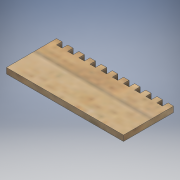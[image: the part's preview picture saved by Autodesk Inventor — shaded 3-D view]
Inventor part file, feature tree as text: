
AUTODESK INVENTOR PART (.ipt)
format: ipt  version: 2017 (Build 210142000, 142)  size: 174,592 bytes
history: native  units: mm
features: extrude x1, sketch x1
ambient origin geometry x8: Origin, YZ Plane, XZ Plane, XY Plane, X Axis, Y Axis, Z Axis, Center Point
bodies: Body1 (feature_tree)
feature tree (2):
  extrude  "Extrusion2"  Depth=6.35mm
  sketch  "Sketch2"  dims[d63=6.35mm d64=6.35mm d65=6.35mm d66=6.35mm d67=6.35mm d68=6.35mm d69=6.35mm d70=6.35mm d71=6.35mm d72=6.35mm d73=6.35mm d74=6.35mm d75=6.35mm d76=6.35mm d77=6.35mm d78=6.35mm d79=6.35mm d80=6.35mm d81=6.35mm d82=6.35mm d83=6.35mm d84=6.35mm d85=6.35mm d86=6.35mm d87=6.35mm d88=6.35mm d89=6.35mm d90=6.35mm d94=6.35mm d95=0.0mm]
